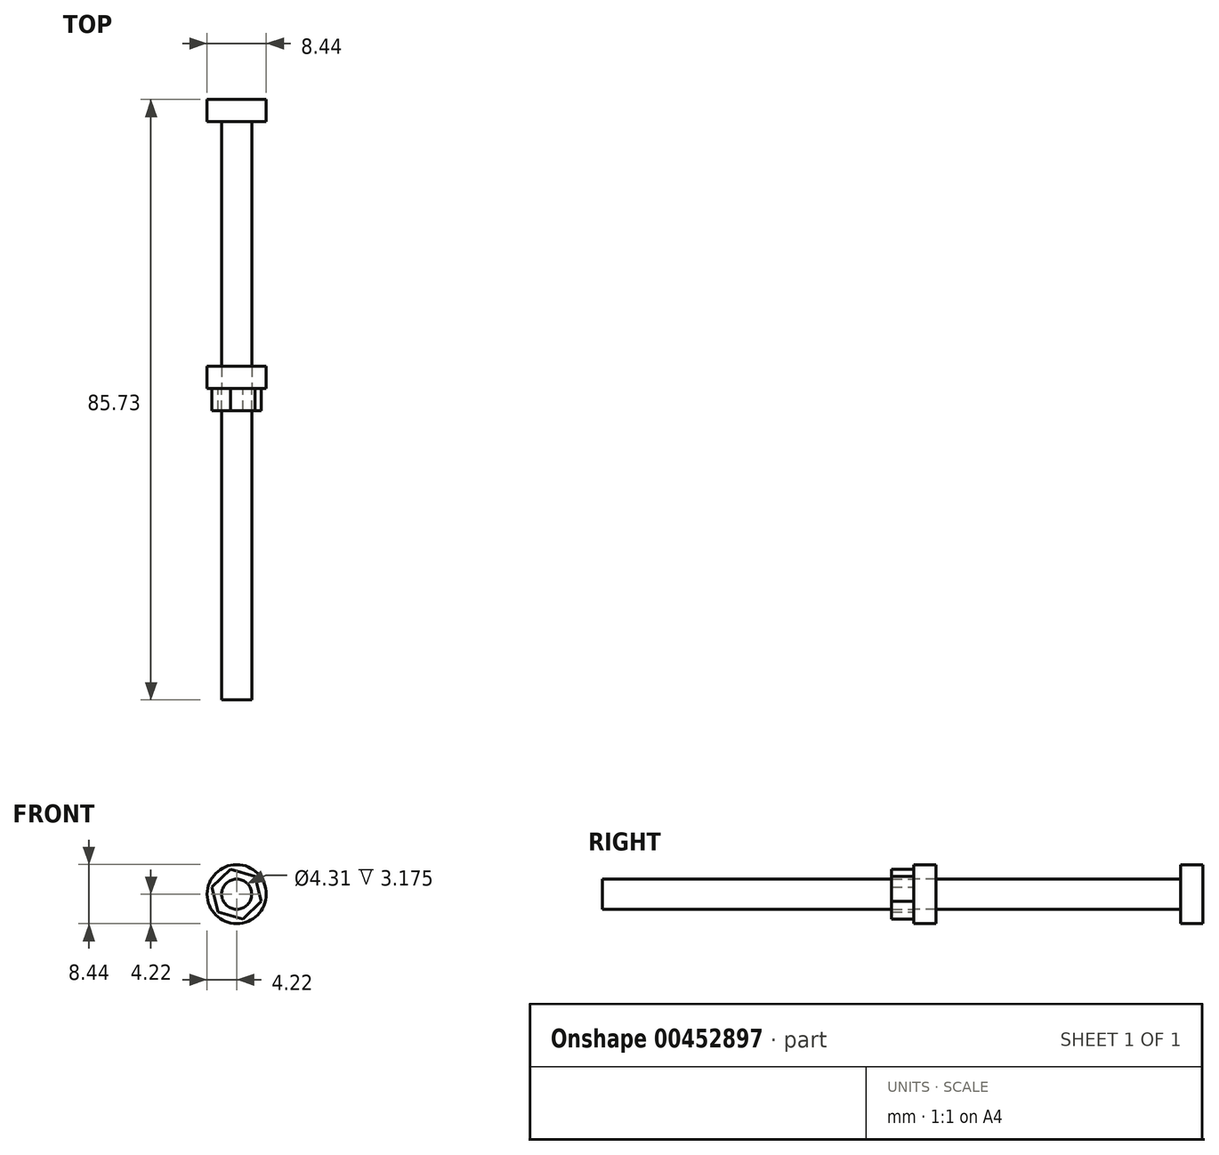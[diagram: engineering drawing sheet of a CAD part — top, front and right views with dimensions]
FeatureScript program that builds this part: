
annotation { "Feature Type Name" : "Feature", "Feature Type Description" : "" }
export const myFeature = defineFeature(function(context is Context, id is Id, definition is map)
    precondition{}
    {
        {
            var Q0;
            Q0=qCreatedBy(makeId("Front.planeOp"),FACE);
            var sketch = newSketch(context, id + "F0", { "sketchPlane" : qUnion([Q0])});
            skCircle(sketch, "E0", {"center": v(0, 0) * mm, "radius": 2.15 * mm});
            skSolve(sketch);
        }
        {
            var Q0;
            Q0=qSketchRegion(id+"F0",true);
            extrude(context, id + "F1", {"entities" : qUnion([Q0]), "depth" : 44.45 * mm});
        }
        {
            var Q0;
            Q0=makeQuery(id+"F1.opExtrude","CAP_FACE",FACE,{"disambiguationData":[OSD([sQuery(id+"F0.wireOp",EDGE,"E0")])],"isStart":true});
            var sketch = newSketch(context, id + "F2", { "sketchPlane" : qUnion([Q0])});
            skCircle(sketch, "E1", {"center": v(0, 0) * mm, "radius": 4.22 * mm});
            skSolve(sketch);
        }
        {
            var Q0;
            Q0=qSketchRegion(id+"F2",true);
            extrude(context, id + "F3", {"entities" : qUnion([Q0]), "operationType" : NewBodyOperationType.ADD, "depth" : 3.17 * mm});
        }
        {
            var Q0;
            Q0=qCreatedBy(makeId("Front.planeOp"),FACE);
            var sketch = newSketch(context, id + "F4", { "sketchPlane" : qUnion([Q0])});
            skCircle(sketch, "E2", {"center": v(0, 0) * mm, "radius": 2.15 * mm});
            skCircle(sketch, "E3.cCircle", {"center": v(0, 0) * mm, "radius": 3.18 * mm, "construction": true});
            skLineSegment(sketch, "E3.0", {"start": v(3.53, -1) * mm, "end": v(0.9, -3.56) * mm});
            skLineSegment(sketch, "E3.1", {"start": v(0.9, -3.56) * mm, "end": v(-2.63, -2.55) * mm});
            skLineSegment(sketch, "E3.2", {"start": v(-2.63, -2.55) * mm, "end": v(-3.53, 1) * mm});
            skLineSegment(sketch, "E3.3", {"start": v(-3.53, 1) * mm, "end": v(-0.9, 3.56) * mm});
            skLineSegment(sketch, "E3.4", {"start": v(-0.9, 3.56) * mm, "end": v(2.63, 2.55) * mm});
            skLineSegment(sketch, "E3.5", {"start": v(2.63, 2.55) * mm, "end": v(3.53, -1) * mm});
            skPoint(sketch, "E3.0.midPoint", {"position": v(2.2, -2.28) * mm});
            skSolve(sketch);
        }
        {
            var Q0;
            Q0=makeQuery(id+"F4.imprint","IMPRINT",FACE,{"disambiguationData":[TD([[makeQuery(id+"F4.imprint","IMPRINT",EDGE,{"derivedFrom":sQuery(id+"F4.wireOp",EDGE,"E2")}),-1.0]])]});
            extrude(context, id + "F5", {"entities" : qUnion([Q0]), "depth" : 3.17 * mm});
        }
        {
            var Q0;
            Q0=qCreatedBy(makeId("Front.planeOp"),FACE);
            var sketch = newSketch(context, id + "F6", { "sketchPlane" : qUnion([Q0])});
            skCircle(sketch, "E4", {"center": v(0, 0) * mm, "radius": 2.15 * mm});
            skSolve(sketch);
        }
        {
            var Q0;
            Q0=qSketchRegion(id+"F6",true);
            extrude(context, id + "F7", {"entities" : qUnion([Q0]), "oppositeDirection" : true, "depth" : 38.1 * mm});
        }
        {
            var Q0;
            Q0=makeQuery(id+"F7.opExtrude","CAP_FACE",FACE,{"disambiguationData":[OSD([sQuery(id+"F6.wireOp",EDGE,"E4")])],"isStart":false});
            var sketch = newSketch(context, id + "F8", { "sketchPlane" : qUnion([Q0])});
            skCircle(sketch, "E5", {"center": v(0, 0) * mm, "radius": 4.22 * mm});
            skSolve(sketch);
        }
        {
            var Q0;
            Q0=qSketchRegion(id+"F8",true);
            extrude(context, id + "F9", {"entities" : qUnion([Q0]), "operationType" : NewBodyOperationType.ADD, "depth" : 3.17 * mm});
        }
    });
